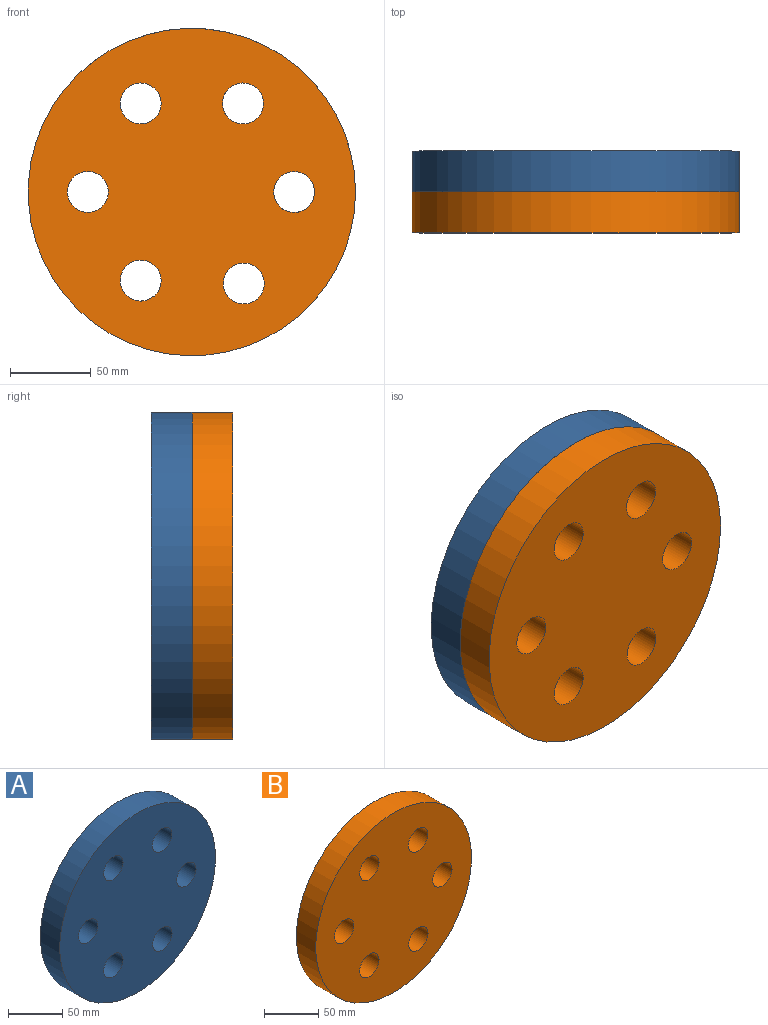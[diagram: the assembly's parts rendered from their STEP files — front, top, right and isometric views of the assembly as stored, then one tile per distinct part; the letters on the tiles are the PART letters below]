
ASSEMBLY  parts=2 mates=1
PART A: 9 faces, bbox 203.2x25.4x203.2 mm
  f0: cylinder r=12.7mm len=25.4mm, axis (0,1,0), area 2026.8mm2, adj f7,f8
  f1: cylinder r=12.7mm len=25.4mm, axis (0,1,0), area 2026.8mm2, adj f7,f8
  f2: cylinder r=12.7mm len=25.4mm, axis (0,1,0), area 2026.8mm2, adj f7,f8
  f3: cylinder r=12.7mm len=25.4mm, axis (0,1,0), area 2026.8mm2, adj f7,f8
  f4: cylinder r=12.7mm len=25.4mm, axis (0,1,0), area 2026.8mm2, adj f7,f8
  f5: cylinder r=12.7mm len=25.4mm, axis (0,1,0), area 2026.8mm2, adj f7,f8
  f6: cylinder r=101.6mm len=203.2mm, axis (0,1,0), area 16214.6mm2, adj f7,f8
  f7: plane 203.2x203.2mm, normal (0,-1,0), area 29389mm2, adj f0,f1,f2,f3,f4,f5,f6
  f8: plane 203.2x203.2mm, normal (0,1,0), area 29389mm2, adj f0,f1,f2,f3,f4,f5,f6
PART B: 9 faces, bbox 203.2x25.4x203.2 mm
  f0: cylinder r=12.7mm len=25.4mm, axis (0,1,0), area 2026.8mm2, adj f7,f8
  f1: cylinder r=12.7mm len=25.4mm, axis (0,1,0), area 2026.8mm2, adj f7,f8
  f2: cylinder r=12.7mm len=25.4mm, axis (0,1,0), area 2026.8mm2, adj f7,f8
  f3: cylinder r=12.7mm len=25.4mm, axis (0,1,0), area 2026.8mm2, adj f7,f8
  f4: cylinder r=12.7mm len=25.4mm, axis (0,1,0), area 2026.8mm2, adj f7,f8
  f5: cylinder r=12.7mm len=25.4mm, axis (0,1,0), area 2026.8mm2, adj f7,f8
  f6: cylinder r=101.6mm len=203.2mm, axis (0,1,0), area 16214.6mm2, adj f7,f8
  f7: plane 203.2x203.2mm, normal (0,-1,0), area 29389mm2, adj f0,f1,f2,f3,f4,f5,f6
  f8: plane 203.2x203.2mm, normal (0,1,0), area 29389mm2, adj f0,f1,f2,f3,f4,f5,f6
PLACE A t=(-19.6,-20.23,-13.33)mm
PLACE B t=(-19.61,-20.23,-13.36)mm
MATE fastened A.f6 <-> B.f8  axis (0,-1,0) through (-19.6,-45.63,-13.33)mm
